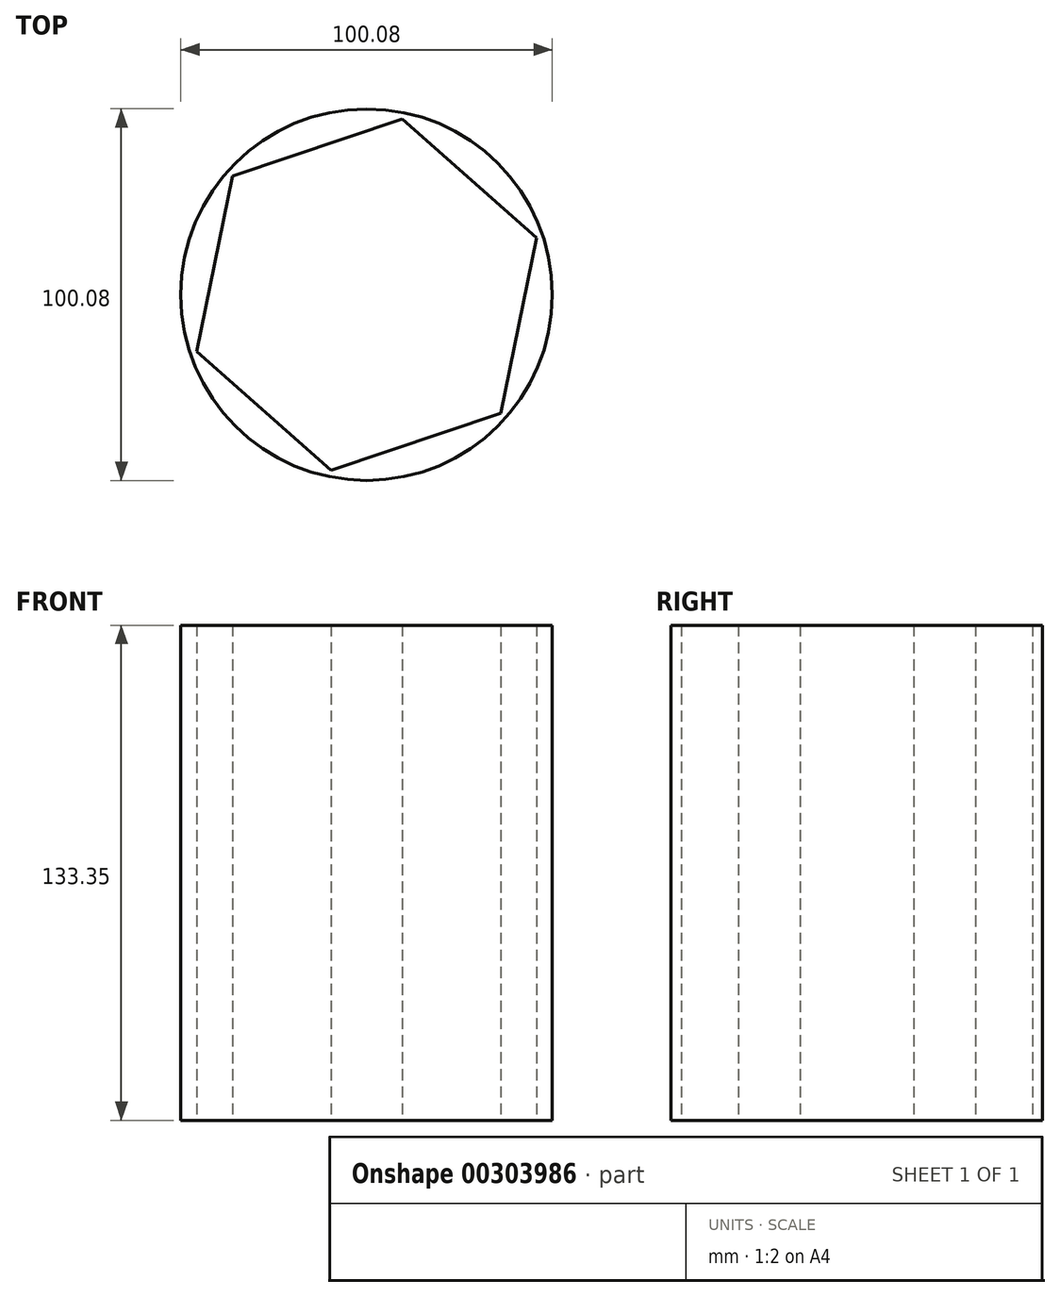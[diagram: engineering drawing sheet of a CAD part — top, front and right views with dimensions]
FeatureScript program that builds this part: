
annotation { "Feature Type Name" : "Feature", "Feature Type Description" : "" }
export const myFeature = defineFeature(function(context is Context, id is Id, definition is map)
    precondition{}
    {
        {
            var Q0;
            Q0=qCreatedBy(makeId("Top.planeOp"),FACE);
            var sketch = newSketch(context, id + "F0", { "sketchPlane" : qUnion([Q0])});
            skCircle(sketch, "E0", {"center": v(0, 0) * mm, "radius": 50.04 * mm});
            skCircle(sketch, "E1.cCircle", {"center": v(0, 0) * mm, "radius": 48.26 * mm, "construction": true});
            skLineSegment(sketch, "E1.0", {"start": v(45.75, 15.36) * mm, "end": v(36.18, -31.94) * mm});
            skLineSegment(sketch, "E1.1", {"start": v(36.18, -31.94) * mm, "end": v(-9.57, -47.3) * mm});
            skLineSegment(sketch, "E1.2", {"start": v(-9.57, -47.3) * mm, "end": v(-45.75, -15.36) * mm});
            skLineSegment(sketch, "E1.3", {"start": v(-45.75, -15.36) * mm, "end": v(-36.18, 31.94) * mm});
            skLineSegment(sketch, "E1.4", {"start": v(-36.18, 31.94) * mm, "end": v(9.57, 47.3) * mm});
            skLineSegment(sketch, "E1.5", {"start": v(9.57, 47.3) * mm, "end": v(45.75, 15.36) * mm});
            skSolve(sketch);
        }
        {
            var Q0;
            Q0 = qSketchRegion(id + "F0", true);
            extrude(context, id + "F1", {"entities" : qUnion([Q0]), "depth" : 133.35 * mm});
        }
    });
